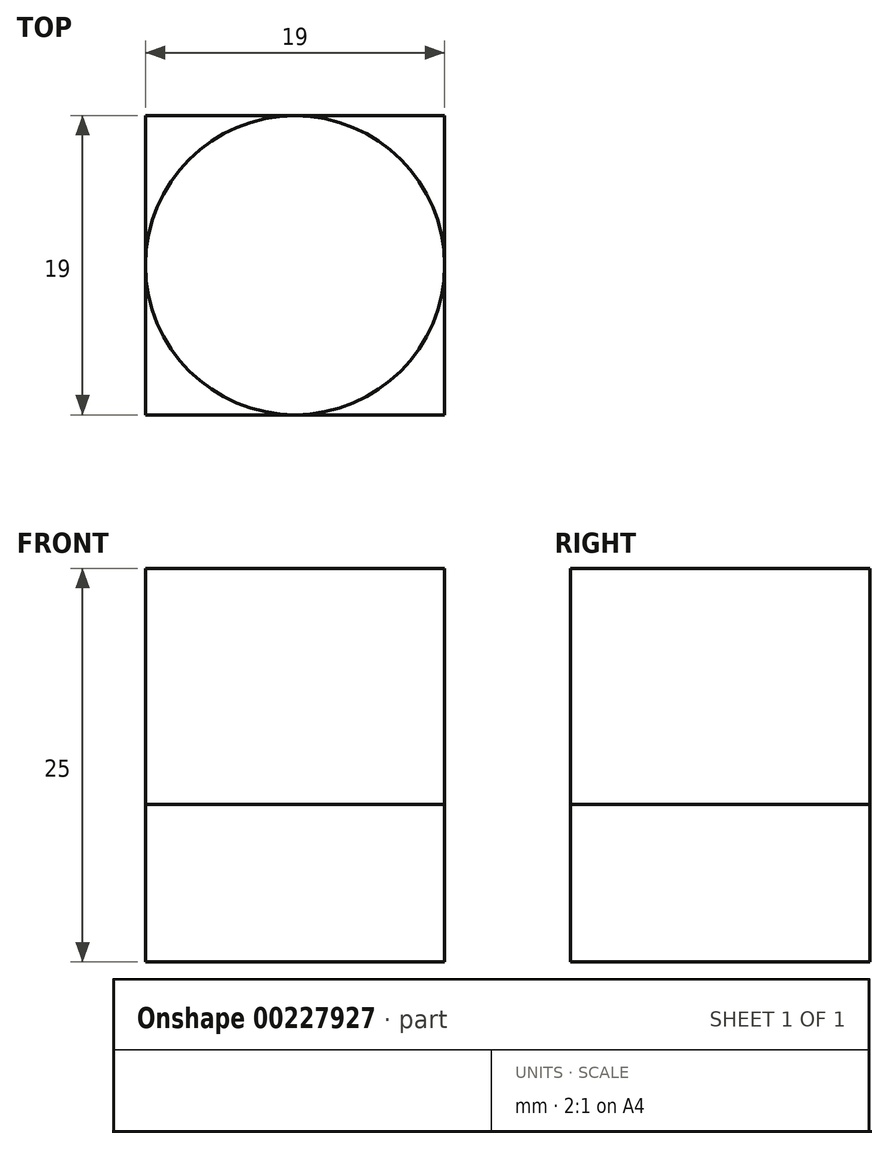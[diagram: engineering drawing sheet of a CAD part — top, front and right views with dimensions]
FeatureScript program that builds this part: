
annotation { "Feature Type Name" : "Feature", "Feature Type Description" : "" }
export const myFeature = defineFeature(function(context is Context, id is Id, definition is map)
    precondition{}
    {
        {
            var Q0;
            Q0=qCreatedBy(makeId("Top.planeOp"),FACE);
            var sketch = newSketch(context, id + "F0", { "sketchPlane" : qUnion([Q0])});
            skLineSegment(sketch, "E0.bottom", {"start": v(-9.5, 9.5) * mm, "end": v(9.5, 9.5) * mm});
            skLineSegment(sketch, "E0.top", {"start": v(-9.5, -9.5) * mm, "end": v(9.5, -9.5) * mm});
            skLineSegment(sketch, "E0.left", {"start": v(-9.5, 9.5) * mm, "end": v(-9.5, -9.5) * mm});
            skLineSegment(sketch, "E0.right", {"start": v(9.5, 9.5) * mm, "end": v(9.5, -9.5) * mm});
            skLineSegment(sketch, "E1", {"start": v(-9.5, 9.5) * mm, "end": v(9.5, -9.5) * mm, "construction": true});
            skSolve(sketch);
        }
        {
            var Q0;
            Q0 = qSketchRegion(id + "F0", true);
            extrude(context, id + "F1", {"entities" : qUnion([Q0]), "depth" : 10 * mm});
        }
        {
            var Q0;
            Q0=makeQuery(id+"F1.opExtrude","CAP_FACE",FACE,{"disambiguationData":[OSD([sQuery(id+"F0.wireOp",EDGE,"E0.bottom"),sQuery(id+"F0.wireOp",EDGE,"E0.top"),sQuery(id+"F0.wireOp",EDGE,"E0.left"),sQuery(id+"F0.wireOp",EDGE,"E0.right")])],"isStart":false});
            var sketch = newSketch(context, id + "F2", { "sketchPlane" : qUnion([Q0])});
            skLineSegment(sketch, "E2", {"start": v(-9.5, 9.5) * mm, "end": v(9.5, -9.5) * mm, "construction": true});
            skCircle(sketch, "E3", {"center": v(0, 0) * mm, "radius": 9.5 * mm});
            skSolve(sketch);
        }
        {
            var Q0;
            {var subQ0=sQuery(id+"F2.wireOp",EDGE,"E3");var subQ1=makeQuery(id+"F2.imprint","INTERSECT",VERTEX,{"derivedFrom":[makeQuery(id+"F1.opExtrude","CAP_EDGE",EDGE,{"disambiguationData":[OSD([sQuery(id+"F0.wireOp",EDGE,"E0.bottom")])],"isStart":false}),subQ0]});Q0=makeQuery(id+"F2.imprint","IMPRINT",FACE,{"disambiguationData":[TD([[makeQuery(id+"F2.imprint","IMPRINT",EDGE,{"disambiguationData":[TD([[subQ1,1.0]])],"derivedFrom":subQ0}),1.0]])]});}
            extrude(context, id + "F3", {"entities" : qUnion([Q0]), "operationType" : NewBodyOperationType.ADD, "depth" : 15 * mm});
        }
    });
